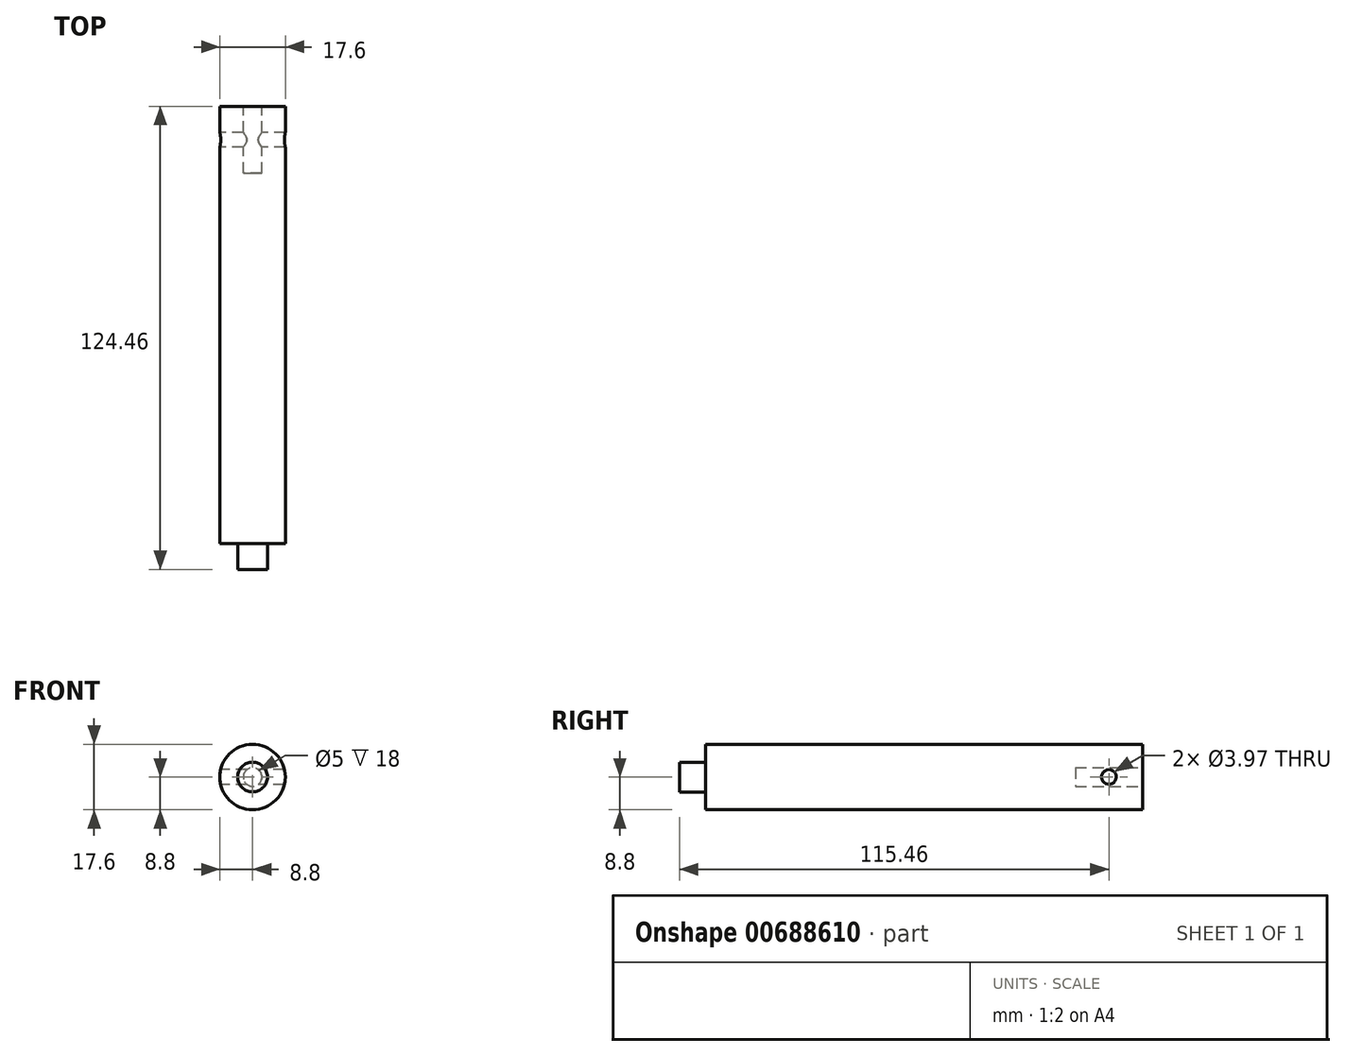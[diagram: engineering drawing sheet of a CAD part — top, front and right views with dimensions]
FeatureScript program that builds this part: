
annotation { "Feature Type Name" : "Feature", "Feature Type Description" : "" }
export const myFeature = defineFeature(function(context is Context, id is Id, definition is map)
    precondition{}
    {
        {
            var Q0;
            Q0=qCreatedBy(makeId("Front.planeOp"),FACE);
            var sketch = newSketch(context, id + "F0", { "sketchPlane" : qUnion([Q0])});
            skCircle(sketch, "E0", {"center": v(0, 0) * mm, "radius": 8.8 * mm});
            skSolve(sketch);
        }
        {
            var Q0;
            Q0=makeQuery(id+"F0.imprint","IMPRINT",FACE,{"disambiguationData":[TD([[makeQuery(id+"F0.imprint","IMPRINT",EDGE,{"derivedFrom":sQuery(id+"F0.wireOp",EDGE,"E0")}),1.0]])]});
            extrude(context, id + "F1", {"entities" : qUnion([Q0]), "depth" : 124.46 * mm, "offsetDistance" : 25.4 * mm});
        }
        {
            var Q0;
            Q0=makeQuery(id+"F1.opExtrude","CAP_FACE",FACE,{"disambiguationData":[OSD([sQuery(id+"F0.wireOp",EDGE,"E0")])],"isStart":false});
            var sketch = newSketch(context, id + "F2", { "sketchPlane" : qUnion([Q0])});
            skPoint(sketch, "E1.0", {"position": v(0, 0) * mm});
            skCircle(sketch, "E2", {"center": v(0, 0) * mm, "radius": 4 * mm});
            skSolve(sketch);
        }
        {
            var Q0;
            Q0=makeQuery(id+"F2.imprint","IMPRINT",FACE,{"disambiguationData":[TD([[makeQuery(id+"F2.imprint","IMPRINT",EDGE,{"derivedFrom":sQuery(id+"F2.wireOp",EDGE,"E2")}),-1.0]])]});
            extrude(context, id + "F3", {"entities" : qUnion([Q0]), "operationType" : NewBodyOperationType.REMOVE, "oppositeDirection" : true, "depth" : 7 * mm, "offsetDistance" : 25.4 * mm});
        }
        {
            var Q0;
            Q0=makeQuery(id+"F1.opExtrude","CAP_FACE",FACE,{"disambiguationData":[OSD([sQuery(id+"F0.wireOp",EDGE,"E0")])],"isStart":true});
            var sketch = newSketch(context, id + "F4", { "sketchPlane" : qUnion([Q0])});
            skCircle(sketch, "E3", {"center": v(0, 0) * mm, "radius": 2.5 * mm});
            skSolve(sketch);
        }
        {
            var Q0;
            Q0=makeQuery(id+"F4.imprint","IMPRINT",FACE,{"disambiguationData":[TD([[makeQuery(id+"F4.imprint","IMPRINT",EDGE,{"derivedFrom":sQuery(id+"F4.wireOp",EDGE,"E3")}),1.0]])]});
            extrude(context, id + "F5", {"entities" : qUnion([Q0]), "operationType" : NewBodyOperationType.REMOVE, "oppositeDirection" : true, "depth" : 18 * mm, "offsetDistance" : 25.4 * mm});
        }
        {
            var Q0;
            Q0=makeQuery(id+"F1.opExtrude","CAP_FACE",FACE,{"disambiguationData":[OSD([sQuery(id+"F0.wireOp",EDGE,"E0")])],"isStart":true});
            var sketch = newSketch(context, id + "F6", { "sketchPlane" : qUnion([Q0])});
            skLineSegment(sketch, "E4", {"start": v(0, 0) * mm, "end": v(8.8, 0) * mm, "construction": true});
            skCircle(sketch, "E5.0", {"center": v(0, 0) * mm, "radius": 8.8 * mm});
            skSolve(sketch);
        }
        {
            var Q0;
            Q0=sQuery(id+"F6.wireOp",VERTEX,"E4.end");
            var Q1;
            Q1=sQuery(id+"F6.wireOp",EDGE,"E4");
            cPlane(context, id + "F7", {"entities" : qUnion([Q0, Q1]), "cplaneType" : CPlaneType.LINE_POINT, "offset" : 25.4 * mm, "width" : 152.4 * mm, "height" : 152.4 * mm});
        }
        {
            var Q0;
            Q0=qCreatedBy(id+"F7.planeOp",FACE);
            var sketch = newSketch(context, id + "F8", { "sketchPlane" : qUnion([Q0])});
            skLineSegment(sketch, "E6", {"start": v(0, 0) * mm, "end": v(28.04, 0) * mm, "construction": true});
            skCircle(sketch, "E7", {"center": v(9, 0) * mm, "radius": 1.98 * mm});
            skSolve(sketch);
        }
        {
            var Q0;
            Q0=makeQuery(id+"F8.imprint","IMPRINT",FACE,{"disambiguationData":[TD([[makeQuery(id+"F8.imprint","IMPRINT",EDGE,{"derivedFrom":sQuery(id+"F8.wireOp",EDGE,"E7")}),1.0]])]});
            extrude(context, id + "F9", {"entities" : qUnion([Q0]), "operationType" : NewBodyOperationType.REMOVE, "endBound" : BoundingType.THROUGH_ALL, "oppositeDirection" : true, "depth" : 25.4 * mm, "offsetDistance" : 25.4 * mm});
        }
    });
